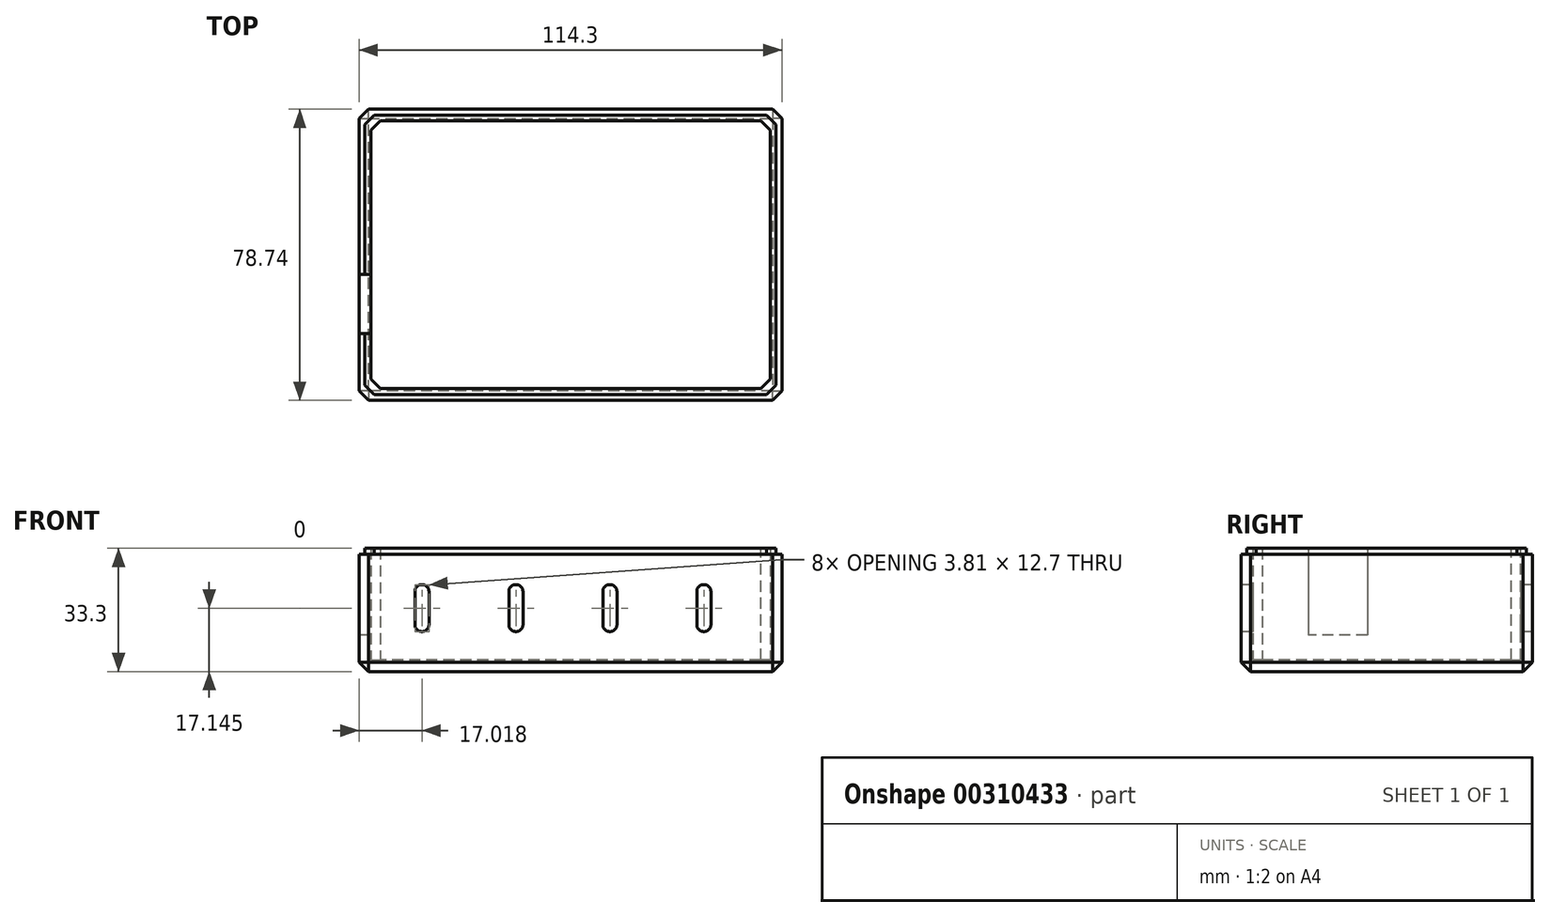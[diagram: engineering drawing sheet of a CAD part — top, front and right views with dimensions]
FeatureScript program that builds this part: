
annotation { "Feature Type Name" : "Feature", "Feature Type Description" : "" }
export const myFeature = defineFeature(function(context is Context, id is Id, definition is map)
    precondition{}
    {
        {
            var Q0;
            Q0=qCreatedBy(makeId("Top.planeOp"),FACE);
            var sketch = newSketch(context, id + "F0", { "sketchPlane" : qUnion([Q0])});
            skLineSegment(sketch, "E0.bottom", {"start": v(57.15, 39.37) * mm, "end": v(-57.15, 39.37) * mm});
            skLineSegment(sketch, "E0.top", {"start": v(57.15, -39.37) * mm, "end": v(-57.15, -39.37) * mm});
            skLineSegment(sketch, "E0.left", {"start": v(57.15, 39.37) * mm, "end": v(57.15, -39.37) * mm});
            skLineSegment(sketch, "E0.right", {"start": v(-57.15, 39.37) * mm, "end": v(-57.15, -39.37) * mm});
            skPoint(sketch, "E0.middle", {"position": v(0, 0) * mm});
            skSolve(sketch);
        }
        {
            var Q0;
            Q0 = qSketchRegion(id + "F0", true);
            extrude(context, id + "F1", {"entities" : qUnion([Q0]), "depth" : 3.17 * mm});
        }
        {
            var Q0;
            Q0=makeQuery(id+"F1.opExtrude","CAP_FACE",FACE,{"disambiguationData":[OSD([sQuery(id+"F0.wireOp",EDGE,"E0.bottom"),sQuery(id+"F0.wireOp",EDGE,"E0.top"),sQuery(id+"F0.wireOp",EDGE,"E0.left"),sQuery(id+"F0.wireOp",EDGE,"E0.right")])],"isStart":false});
            var sketch = newSketch(context, id + "F2", { "sketchPlane" : qUnion([Q0])});
            skLineSegment(sketch, "E1.0", {"start": v(53.98, 36.2) * mm, "end": v(-53.98, 36.2) * mm});
            skLineSegment(sketch, "E1.1", {"start": v(53.98, 36.2) * mm, "end": v(53.98, -36.2) * mm});
            skLineSegment(sketch, "E1.2", {"start": v(53.98, -36.2) * mm, "end": v(-53.98, -36.2) * mm});
            skLineSegment(sketch, "E1.3", {"start": v(-53.98, 36.2) * mm, "end": v(-53.98, -36.2) * mm});
            skSolve(sketch);
        }
        {
            var Q0;
            Q0=makeQuery(id+"F2.imprint","IMPRINT",FACE,{"disambiguationData":[TD([[makeQuery(id+"F2.imprint","IMPRINT",EDGE,{"derivedFrom":sQuery(id+"F2.wireOp",EDGE,"E1.0")}),-1.0]])]});
            extrude(context, id + "F3", {"entities" : qUnion([Q0]), "operationType" : NewBodyOperationType.ADD, "depth" : 28.57 * mm});
        }
        {
            var Q0;
            {var subQ0=sQuery(id+"F0.wireOp",EDGE,"E0.right");Q0=makeQuery(id+"F3.boolean.opBoolean","MERGE",FACE,{"derivedFrom":[makeQuery(id+"F1.opExtrude","SWEPT_FACE",FACE,{"disambiguationData":[OSD([subQ0])]}),makeQuery(id+"F3.opExtrude","SWEPT_FACE",FACE,{"disambiguationData":[OSD([subQ0])]})]});}
            var sketch = newSketch(context, id + "F4", { "sketchPlane" : qUnion([Q0])});
            skPoint(sketch, "E2", {"position": v(13.23, 20.83) * mm});
            skLineSegment(sketch, "E3.bottom", {"start": v(5.23, 31.75) * mm, "end": v(21.23, 31.75) * mm});
            skLineSegment(sketch, "E3.top", {"start": v(5.23, 9.9) * mm, "end": v(21.23, 9.9) * mm});
            skLineSegment(sketch, "E3.left", {"start": v(5.23, 31.75) * mm, "end": v(5.23, 9.9) * mm});
            skLineSegment(sketch, "E3.right", {"start": v(21.23, 31.75) * mm, "end": v(21.23, 9.9) * mm});
            skSolve(sketch);
        }
        {
            var Q0;
            Q0=makeQuery(id+"F4.imprint","IMPRINT",FACE,{"disambiguationData":[TD([[makeQuery(id+"F4.imprint","IMPRINT",EDGE,{"derivedFrom":sQuery(id+"F4.wireOp",EDGE,"E3.bottom")}),-1.0]])]});
            extrude(context, id + "F5", {"entities" : qUnion([Q0]), "operationType" : NewBodyOperationType.REMOVE, "endBound" : BoundingType.UP_TO_NEXT, "oppositeDirection" : true, "depth" : 25.4 * mm});
        }
        {
            var Q0;
            Q0=makeQuery(id+"F3.opExtrude","CAP_FACE",FACE,{"disambiguationData":[OSD([sQuery(id+"F0.wireOp",EDGE,"E0.bottom"),sQuery(id+"F0.wireOp",EDGE,"E0.top"),sQuery(id+"F0.wireOp",EDGE,"E0.left"),sQuery(id+"F0.wireOp",EDGE,"E0.right"),sQuery(id+"F2.wireOp",EDGE,"E1.0"),sQuery(id+"F2.wireOp",EDGE,"E1.1"),sQuery(id+"F2.wireOp",EDGE,"E1.2"),sQuery(id+"F2.wireOp",EDGE,"E1.3")])],"isStart":false});
            var sketch = newSketch(context, id + "F6", { "sketchPlane" : qUnion([Q0])});
            skLineSegment(sketch, "E4.0", {"start": v(-55.55, 37.77) * mm, "end": v(-55.55, -5.23) * mm});
            skLineSegment(sketch, "E4.1", {"start": v(-55.55, -21.23) * mm, "end": v(-55.55, -37.77) * mm});
            skLineSegment(sketch, "E4.2", {"start": v(55.55, -37.77) * mm, "end": v(-55.55, -37.77) * mm});
            skLineSegment(sketch, "E4.3", {"start": v(55.55, 37.77) * mm, "end": v(55.55, -37.77) * mm});
            skLineSegment(sketch, "E4.4", {"start": v(55.55, 37.77) * mm, "end": v(-55.55, 37.77) * mm});
            skSolve(sketch);
        }
        {
            var Q0;
            {var subQ10=sQuery(id+"F6.wireOp",EDGE,"E4.0");Q0=makeQuery(id+"F6.imprint","IMPRINT",FACE,{"disambiguationData":[TD([[makeQuery(id+"F6.imprint","IMPRINT",EDGE,{"derivedFrom":subQ10}),1.0]])]});}
            extrude(context, id + "F7", {"entities" : qUnion([Q0]), "operationType" : NewBodyOperationType.ADD, "depth" : 1.55 * mm});
        }
        {
            var Q0;
            {var subQ0=sQuery(id+"F0.wireOp",EDGE,"E0.left");var subQ1=sQuery(id+"F0.wireOp",EDGE,"E0.bottom");Q0=makeQuery(id+"F3.boolean.opBoolean","MERGE",EDGE,{"derivedFrom":[makeQuery(id+"F1.opExtrude","SWEPT_EDGE",EDGE,{"disambiguationData":[OSD([subQ1,subQ0])]}),makeQuery(id+"F3.opExtrude","SWEPT_EDGE",EDGE,{"disambiguationData":[OSD([subQ1,subQ0])]})]});}
            var Q1;
            {var subQ0=sQuery(id+"F0.wireOp",EDGE,"E0.left");var subQ1=sQuery(id+"F0.wireOp",EDGE,"E0.top");Q1=makeQuery(id+"F3.boolean.opBoolean","MERGE",EDGE,{"derivedFrom":[makeQuery(id+"F1.opExtrude","SWEPT_EDGE",EDGE,{"disambiguationData":[OSD([subQ1,subQ0])]}),makeQuery(id+"F3.opExtrude","SWEPT_EDGE",EDGE,{"disambiguationData":[OSD([subQ1,subQ0])]})]});}
            var Q2;
            {var subQ0=sQuery(id+"F0.wireOp",EDGE,"E0.right");var subQ1=sQuery(id+"F0.wireOp",EDGE,"E0.top");Q2=makeQuery(id+"F3.boolean.opBoolean","MERGE",EDGE,{"derivedFrom":[makeQuery(id+"F1.opExtrude","SWEPT_EDGE",EDGE,{"disambiguationData":[OSD([subQ1,subQ0])]}),makeQuery(id+"F3.opExtrude","SWEPT_EDGE",EDGE,{"disambiguationData":[OSD([subQ1,subQ0])]})]});}
            var Q3;
            {var subQ0=sQuery(id+"F0.wireOp",EDGE,"E0.right");var subQ1=sQuery(id+"F0.wireOp",EDGE,"E0.bottom");Q3=makeQuery(id+"F3.boolean.opBoolean","MERGE",EDGE,{"derivedFrom":[makeQuery(id+"F1.opExtrude","SWEPT_EDGE",EDGE,{"disambiguationData":[OSD([subQ1,subQ0])]}),makeQuery(id+"F3.opExtrude","SWEPT_EDGE",EDGE,{"disambiguationData":[OSD([subQ1,subQ0])]})]});}
            var Q4;
            Q4=makeQuery(id+"F1.opExtrude","CAP_EDGE",EDGE,{"disambiguationData":[OSD([sQuery(id+"F0.wireOp",EDGE,"E0.bottom")])],"isStart":true});
            var Q5;
            Q5=makeQuery(id+"F1.opExtrude","CAP_EDGE",EDGE,{"disambiguationData":[OSD([sQuery(id+"F0.wireOp",EDGE,"E0.right")])],"isStart":true});
            var Q6;
            Q6=makeQuery(id+"F1.opExtrude","CAP_EDGE",EDGE,{"disambiguationData":[OSD([sQuery(id+"F0.wireOp",EDGE,"E0.top")])],"isStart":true});
            var Q7;
            Q7=makeQuery(id+"F1.opExtrude","CAP_EDGE",EDGE,{"disambiguationData":[OSD([sQuery(id+"F0.wireOp",EDGE,"E0.left")])],"isStart":true});
            chamfer(context, id + "F8", {"entities" : qUnion([Q0, Q1, Q2, Q3, Q4, Q5, Q6, Q7]), "width" : 2.54 * mm, "tangentPropagation" : true});
        }
        {
            var Q0;
            {var subQ0=sQuery(id+"F2.wireOp",EDGE,"E1.3");var subQ1=sQuery(id+"F2.wireOp",EDGE,"E1.0");Q0=makeQuery(id+"F7.boolean.opBoolean","MERGE",EDGE,{"derivedFrom":[makeQuery(id+"F3.opExtrude","SWEPT_EDGE",EDGE,{"disambiguationData":[OSD([subQ1,subQ0])]}),makeQuery(id+"F7.opExtrude","SWEPT_EDGE",EDGE,{"disambiguationData":[OSD([subQ1,subQ0])]})]});}
            var Q1;
            {var subQ0=sQuery(id+"F2.wireOp",EDGE,"E1.1");var subQ1=sQuery(id+"F2.wireOp",EDGE,"E1.0");Q1=makeQuery(id+"F7.boolean.opBoolean","MERGE",EDGE,{"derivedFrom":[makeQuery(id+"F3.opExtrude","SWEPT_EDGE",EDGE,{"disambiguationData":[OSD([subQ1,subQ0])]}),makeQuery(id+"F7.opExtrude","SWEPT_EDGE",EDGE,{"disambiguationData":[OSD([subQ1,subQ0])]})]});}
            var Q2;
            {var subQ0=sQuery(id+"F2.wireOp",EDGE,"E1.2");var subQ1=sQuery(id+"F2.wireOp",EDGE,"E1.1");Q2=makeQuery(id+"F7.boolean.opBoolean","MERGE",EDGE,{"derivedFrom":[makeQuery(id+"F3.opExtrude","SWEPT_EDGE",EDGE,{"disambiguationData":[OSD([subQ1,subQ0])]}),makeQuery(id+"F7.opExtrude","SWEPT_EDGE",EDGE,{"disambiguationData":[OSD([subQ1,subQ0])]})]});}
            var Q3;
            {var subQ0=sQuery(id+"F2.wireOp",EDGE,"E1.3");var subQ1=sQuery(id+"F2.wireOp",EDGE,"E1.2");Q3=makeQuery(id+"F7.boolean.opBoolean","MERGE",EDGE,{"derivedFrom":[makeQuery(id+"F3.opExtrude","SWEPT_EDGE",EDGE,{"disambiguationData":[OSD([subQ1,subQ0])]}),makeQuery(id+"F7.opExtrude","SWEPT_EDGE",EDGE,{"disambiguationData":[OSD([subQ1,subQ0])]})]});}
            chamfer(context, id + "F9", {"entities" : qUnion([Q0, Q1, Q2, Q3]), "width" : 2.54 * mm, "tangentPropagation" : true});
        }
        {
            var Q0;
            Q0=makeQuery(id+"F7.opExtrude","SWEPT_EDGE",EDGE,{"disambiguationData":[OSD([sQuery(id+"F6.wireOp",EDGE,"E4.3"),sQuery(id+"F6.wireOp",EDGE,"E4.4")])]});
            var Q1;
            Q1=makeQuery(id+"F7.opExtrude","SWEPT_EDGE",EDGE,{"disambiguationData":[OSD([sQuery(id+"F6.wireOp",EDGE,"E4.0"),sQuery(id+"F6.wireOp",EDGE,"E4.4")])]});
            var Q2;
            Q2=makeQuery(id+"F7.opExtrude","SWEPT_EDGE",EDGE,{"disambiguationData":[OSD([sQuery(id+"F6.wireOp",EDGE,"E4.1"),sQuery(id+"F6.wireOp",EDGE,"E4.2")])]});
            var Q3;
            Q3=makeQuery(id+"F7.opExtrude","SWEPT_EDGE",EDGE,{"disambiguationData":[OSD([sQuery(id+"F6.wireOp",EDGE,"E4.2"),sQuery(id+"F6.wireOp",EDGE,"E4.3")])]});
            chamfer(context, id + "F10", {"entities" : qUnion([Q0, Q1, Q2, Q3]), "width" : 2.54 * mm, "tangentPropagation" : true});
        }
        {
            var Q0;
            {var subQ0=sQuery(id+"F0.wireOp",EDGE,"E0.top");Q0=makeQuery(id+"F3.boolean.opBoolean","MERGE",FACE,{"derivedFrom":[makeQuery(id+"F1.opExtrude","SWEPT_FACE",FACE,{"disambiguationData":[OSD([subQ0])]}),makeQuery(id+"F3.opExtrude","SWEPT_FACE",FACE,{"disambiguationData":[OSD([subQ0])]})]});}
            var sketch = newSketch(context, id + "F11", { "sketchPlane" : qUnion([Q0])});
            skPoint(sketch, "E5", {"position": v(-40.13, 17.14) * mm});
            skPoint(sketch, "E6", {"position": v(-14.73, 17.14) * mm});
            skPoint(sketch, "E7", {"position": v(10.67, 17.14) * mm});
            skPoint(sketch, "E8", {"position": v(36.07, 17.14) * mm});
            skLineSegment(sketch, "E9.bottom", {"start": v(-42.04, 23.5) * mm, "end": v(-38.23, 23.5) * mm});
            skLineSegment(sketch, "E9.top", {"start": v(-42.04, 10.8) * mm, "end": v(-38.23, 10.8) * mm});
            skLineSegment(sketch, "E9.left", {"start": v(-42.04, 23.5) * mm, "end": v(-42.04, 10.8) * mm});
            skLineSegment(sketch, "E9.right", {"start": v(-38.23, 23.5) * mm, "end": v(-38.23, 10.8) * mm});
            skLineSegment(sketch, "E10.bottom", {"start": v(-16.64, 23.5) * mm, "end": v(-12.83, 23.5) * mm});
            skLineSegment(sketch, "E10.top", {"start": v(-16.64, 10.8) * mm, "end": v(-12.83, 10.8) * mm});
            skLineSegment(sketch, "E10.left", {"start": v(-16.64, 23.5) * mm, "end": v(-16.64, 10.8) * mm});
            skLineSegment(sketch, "E10.right", {"start": v(-12.83, 23.5) * mm, "end": v(-12.83, 10.8) * mm});
            skLineSegment(sketch, "E11.bottom", {"start": v(8.76, 23.5) * mm, "end": v(12.57, 23.5) * mm});
            skLineSegment(sketch, "E11.top", {"start": v(8.76, 10.8) * mm, "end": v(12.57, 10.8) * mm});
            skLineSegment(sketch, "E11.left", {"start": v(8.76, 23.5) * mm, "end": v(8.76, 10.8) * mm});
            skLineSegment(sketch, "E11.right", {"start": v(12.57, 23.5) * mm, "end": v(12.57, 10.8) * mm});
            skLineSegment(sketch, "E12.bottom", {"start": v(34.16, 23.5) * mm, "end": v(37.97, 23.5) * mm});
            skLineSegment(sketch, "E12.top", {"start": v(34.16, 10.8) * mm, "end": v(37.97, 10.8) * mm});
            skLineSegment(sketch, "E12.left", {"start": v(34.16, 23.5) * mm, "end": v(34.16, 10.8) * mm});
            skLineSegment(sketch, "E12.right", {"start": v(37.97, 23.5) * mm, "end": v(37.97, 10.8) * mm});
            skSolve(sketch);
        }
        {
            var Q0;
            Q0=makeQuery(id+"F11.imprint","IMPRINT",FACE,{"disambiguationData":[TD([[makeQuery(id+"F11.imprint","IMPRINT",EDGE,{"derivedFrom":sQuery(id+"F11.wireOp",EDGE,"E9.bottom")}),-1.0]])]});
            var Q1;
            Q1=makeQuery(id+"F11.imprint","IMPRINT",FACE,{"disambiguationData":[TD([[makeQuery(id+"F11.imprint","IMPRINT",EDGE,{"derivedFrom":sQuery(id+"F11.wireOp",EDGE,"E10.bottom")}),-1.0]])]});
            var Q2;
            Q2=makeQuery(id+"F11.imprint","IMPRINT",FACE,{"disambiguationData":[TD([[makeQuery(id+"F11.imprint","IMPRINT",EDGE,{"derivedFrom":sQuery(id+"F11.wireOp",EDGE,"E11.bottom")}),-1.0]])]});
            var Q3;
            Q3=makeQuery(id+"F11.imprint","IMPRINT",FACE,{"disambiguationData":[TD([[makeQuery(id+"F11.imprint","IMPRINT",EDGE,{"derivedFrom":sQuery(id+"F11.wireOp",EDGE,"E12.bottom")}),-1.0]])]});
            extrude(context, id + "F12", {"entities" : qUnion([Q0, Q1, Q2, Q3]), "operationType" : NewBodyOperationType.REMOVE, "endBound" : BoundingType.THROUGH_ALL, "oppositeDirection" : true, "depth" : 25.4 * mm});
        }
        {
            var Q0;
            {var subQ1=sQuery(id+"F0.wireOp",EDGE,"E0.top");var subQ2=sQuery(id+"F11.wireOp",EDGE,"E9.bottom");var subQ3=sQuery(id+"F11.wireOp",EDGE,"E9.left");Q0=makeQuery(id+"F12.boolean.opBoolean","COPY",EDGE,{"disambiguationData":[TD([makeQuery(id+"F1.opExtrude","SWEPT_FACE",FACE,{"disambiguationData":[OSD([subQ1])]})])],"derivedFrom":makeQuery(id+"F12.opExtrude","SWEPT_EDGE",EDGE,{"disambiguationData":[OSD([subQ2,subQ3])]})});}
            var Q1;
            {var subQ1=sQuery(id+"F0.wireOp",EDGE,"E0.top");var subQ2=sQuery(id+"F11.wireOp",EDGE,"E10.left");var subQ3=sQuery(id+"F11.wireOp",EDGE,"E10.bottom");Q1=makeQuery(id+"F12.boolean.opBoolean","COPY",EDGE,{"disambiguationData":[TD([makeQuery(id+"F1.opExtrude","SWEPT_FACE",FACE,{"disambiguationData":[OSD([subQ1])]})])],"derivedFrom":makeQuery(id+"F12.opExtrude","SWEPT_EDGE",EDGE,{"disambiguationData":[OSD([subQ3,subQ2])]})});}
            var Q2;
            {var subQ1=sQuery(id+"F0.wireOp",EDGE,"E0.top");var subQ2=sQuery(id+"F11.wireOp",EDGE,"E11.bottom");var subQ3=sQuery(id+"F11.wireOp",EDGE,"E11.left");Q2=makeQuery(id+"F12.boolean.opBoolean","COPY",EDGE,{"disambiguationData":[TD([makeQuery(id+"F1.opExtrude","SWEPT_FACE",FACE,{"disambiguationData":[OSD([subQ1])]})])],"derivedFrom":makeQuery(id+"F12.opExtrude","SWEPT_EDGE",EDGE,{"disambiguationData":[OSD([subQ2,subQ3])]})});}
            var Q3;
            {var subQ1=sQuery(id+"F0.wireOp",EDGE,"E0.top");var subQ2=sQuery(id+"F11.wireOp",EDGE,"E12.bottom");var subQ3=sQuery(id+"F11.wireOp",EDGE,"E12.left");Q3=makeQuery(id+"F12.boolean.opBoolean","COPY",EDGE,{"disambiguationData":[TD([makeQuery(id+"F1.opExtrude","SWEPT_FACE",FACE,{"disambiguationData":[OSD([subQ1])]})])],"derivedFrom":makeQuery(id+"F12.opExtrude","SWEPT_EDGE",EDGE,{"disambiguationData":[OSD([subQ2,subQ3])]})});}
            var Q4;
            {var subQ1=sQuery(id+"F0.wireOp",EDGE,"E0.top");var subQ2=sQuery(id+"F11.wireOp",EDGE,"E9.bottom");var subQ3=sQuery(id+"F11.wireOp",EDGE,"E9.right");Q4=makeQuery(id+"F12.boolean.opBoolean","COPY",EDGE,{"disambiguationData":[TD([makeQuery(id+"F1.opExtrude","SWEPT_FACE",FACE,{"disambiguationData":[OSD([subQ1])]})])],"derivedFrom":makeQuery(id+"F12.opExtrude","SWEPT_EDGE",EDGE,{"disambiguationData":[OSD([subQ2,subQ3])]})});}
            var Q5;
            {var subQ1=sQuery(id+"F0.wireOp",EDGE,"E0.top");var subQ2=sQuery(id+"F11.wireOp",EDGE,"E10.bottom");var subQ3=sQuery(id+"F11.wireOp",EDGE,"E10.right");Q5=makeQuery(id+"F12.boolean.opBoolean","COPY",EDGE,{"disambiguationData":[TD([makeQuery(id+"F1.opExtrude","SWEPT_FACE",FACE,{"disambiguationData":[OSD([subQ1])]})])],"derivedFrom":makeQuery(id+"F12.opExtrude","SWEPT_EDGE",EDGE,{"disambiguationData":[OSD([subQ2,subQ3])]})});}
            var Q6;
            {var subQ1=sQuery(id+"F0.wireOp",EDGE,"E0.top");var subQ2=sQuery(id+"F11.wireOp",EDGE,"E11.bottom");var subQ3=sQuery(id+"F11.wireOp",EDGE,"E11.right");Q6=makeQuery(id+"F12.boolean.opBoolean","COPY",EDGE,{"disambiguationData":[TD([makeQuery(id+"F1.opExtrude","SWEPT_FACE",FACE,{"disambiguationData":[OSD([subQ1])]})])],"derivedFrom":makeQuery(id+"F12.opExtrude","SWEPT_EDGE",EDGE,{"disambiguationData":[OSD([subQ2,subQ3])]})});}
            var Q7;
            {var subQ1=sQuery(id+"F0.wireOp",EDGE,"E0.top");var subQ2=sQuery(id+"F11.wireOp",EDGE,"E12.bottom");var subQ3=sQuery(id+"F11.wireOp",EDGE,"E12.right");Q7=makeQuery(id+"F12.boolean.opBoolean","COPY",EDGE,{"disambiguationData":[TD([makeQuery(id+"F1.opExtrude","SWEPT_FACE",FACE,{"disambiguationData":[OSD([subQ1])]})])],"derivedFrom":makeQuery(id+"F12.opExtrude","SWEPT_EDGE",EDGE,{"disambiguationData":[OSD([subQ2,subQ3])]})});}
            var Q8;
            {var subQ1=sQuery(id+"F11.wireOp",EDGE,"E9.top");var subQ2=sQuery(id+"F0.wireOp",EDGE,"E0.top");var subQ3=sQuery(id+"F11.wireOp",EDGE,"E9.left");Q8=makeQuery(id+"F12.boolean.opBoolean","COPY",EDGE,{"disambiguationData":[TD([makeQuery(id+"F1.opExtrude","SWEPT_FACE",FACE,{"disambiguationData":[OSD([subQ2])]})])],"derivedFrom":makeQuery(id+"F12.opExtrude","SWEPT_EDGE",EDGE,{"disambiguationData":[OSD([subQ1,subQ3])]})});}
            var Q9;
            {var subQ1=sQuery(id+"F0.wireOp",EDGE,"E0.top");var subQ2=sQuery(id+"F11.wireOp",EDGE,"E10.left");var subQ3=sQuery(id+"F11.wireOp",EDGE,"E10.top");Q9=makeQuery(id+"F12.boolean.opBoolean","COPY",EDGE,{"disambiguationData":[TD([makeQuery(id+"F1.opExtrude","SWEPT_FACE",FACE,{"disambiguationData":[OSD([subQ1])]})])],"derivedFrom":makeQuery(id+"F12.opExtrude","SWEPT_EDGE",EDGE,{"disambiguationData":[OSD([subQ3,subQ2])]})});}
            var Q10;
            {var subQ1=sQuery(id+"F0.wireOp",EDGE,"E0.top");var subQ2=sQuery(id+"F11.wireOp",EDGE,"E11.top");var subQ3=sQuery(id+"F11.wireOp",EDGE,"E11.left");Q10=makeQuery(id+"F12.boolean.opBoolean","COPY",EDGE,{"disambiguationData":[TD([makeQuery(id+"F1.opExtrude","SWEPT_FACE",FACE,{"disambiguationData":[OSD([subQ1])]})])],"derivedFrom":makeQuery(id+"F12.opExtrude","SWEPT_EDGE",EDGE,{"disambiguationData":[OSD([subQ2,subQ3])]})});}
            var Q11;
            {var subQ1=sQuery(id+"F0.wireOp",EDGE,"E0.top");var subQ2=sQuery(id+"F11.wireOp",EDGE,"E12.top");var subQ3=sQuery(id+"F11.wireOp",EDGE,"E12.left");Q11=makeQuery(id+"F12.boolean.opBoolean","COPY",EDGE,{"disambiguationData":[TD([makeQuery(id+"F1.opExtrude","SWEPT_FACE",FACE,{"disambiguationData":[OSD([subQ1])]})])],"derivedFrom":makeQuery(id+"F12.opExtrude","SWEPT_EDGE",EDGE,{"disambiguationData":[OSD([subQ2,subQ3])]})});}
            var Q12;
            {var subQ1=sQuery(id+"F11.wireOp",EDGE,"E9.top");var subQ2=sQuery(id+"F0.wireOp",EDGE,"E0.top");var subQ3=sQuery(id+"F11.wireOp",EDGE,"E9.right");Q12=makeQuery(id+"F12.boolean.opBoolean","COPY",EDGE,{"disambiguationData":[TD([makeQuery(id+"F1.opExtrude","SWEPT_FACE",FACE,{"disambiguationData":[OSD([subQ2])]})])],"derivedFrom":makeQuery(id+"F12.opExtrude","SWEPT_EDGE",EDGE,{"disambiguationData":[OSD([subQ1,subQ3])]})});}
            var Q13;
            {var subQ1=sQuery(id+"F0.wireOp",EDGE,"E0.top");var subQ2=sQuery(id+"F11.wireOp",EDGE,"E10.top");var subQ3=sQuery(id+"F11.wireOp",EDGE,"E10.right");Q13=makeQuery(id+"F12.boolean.opBoolean","COPY",EDGE,{"disambiguationData":[TD([makeQuery(id+"F1.opExtrude","SWEPT_FACE",FACE,{"disambiguationData":[OSD([subQ1])]})])],"derivedFrom":makeQuery(id+"F12.opExtrude","SWEPT_EDGE",EDGE,{"disambiguationData":[OSD([subQ2,subQ3])]})});}
            var Q14;
            {var subQ1=sQuery(id+"F0.wireOp",EDGE,"E0.top");var subQ2=sQuery(id+"F11.wireOp",EDGE,"E11.top");var subQ3=sQuery(id+"F11.wireOp",EDGE,"E11.right");Q14=makeQuery(id+"F12.boolean.opBoolean","COPY",EDGE,{"disambiguationData":[TD([makeQuery(id+"F1.opExtrude","SWEPT_FACE",FACE,{"disambiguationData":[OSD([subQ1])]})])],"derivedFrom":makeQuery(id+"F12.opExtrude","SWEPT_EDGE",EDGE,{"disambiguationData":[OSD([subQ2,subQ3])]})});}
            var Q15;
            {var subQ1=sQuery(id+"F0.wireOp",EDGE,"E0.top");var subQ2=sQuery(id+"F11.wireOp",EDGE,"E12.top");var subQ3=sQuery(id+"F11.wireOp",EDGE,"E12.right");Q15=makeQuery(id+"F12.boolean.opBoolean","COPY",EDGE,{"disambiguationData":[TD([makeQuery(id+"F1.opExtrude","SWEPT_FACE",FACE,{"disambiguationData":[OSD([subQ1])]})])],"derivedFrom":makeQuery(id+"F12.opExtrude","SWEPT_EDGE",EDGE,{"disambiguationData":[OSD([subQ2,subQ3])]})});}
            var Q16;
            {var subQ0=sQuery(id+"F0.wireOp",EDGE,"E0.bottom");var subQ2=sQuery(id+"F11.wireOp",EDGE,"E12.right");var subQ3=sQuery(id+"F11.wireOp",EDGE,"E12.bottom");Q16=makeQuery(id+"F12.boolean.opBoolean","COPY",EDGE,{"disambiguationData":[TD([makeQuery(id+"F1.opExtrude","SWEPT_FACE",FACE,{"disambiguationData":[OSD([subQ0])]})])],"derivedFrom":makeQuery(id+"F12.opExtrude","SWEPT_EDGE",EDGE,{"disambiguationData":[OSD([subQ3,subQ2])]})});}
            var Q17;
            {var subQ0=sQuery(id+"F0.wireOp",EDGE,"E0.bottom");var subQ2=sQuery(id+"F11.wireOp",EDGE,"E11.bottom");var subQ3=sQuery(id+"F11.wireOp",EDGE,"E11.right");Q17=makeQuery(id+"F12.boolean.opBoolean","COPY",EDGE,{"disambiguationData":[TD([makeQuery(id+"F1.opExtrude","SWEPT_FACE",FACE,{"disambiguationData":[OSD([subQ0])]})])],"derivedFrom":makeQuery(id+"F12.opExtrude","SWEPT_EDGE",EDGE,{"disambiguationData":[OSD([subQ2,subQ3])]})});}
            var Q18;
            {var subQ0=sQuery(id+"F0.wireOp",EDGE,"E0.bottom");var subQ2=sQuery(id+"F11.wireOp",EDGE,"E10.bottom");var subQ3=sQuery(id+"F11.wireOp",EDGE,"E10.right");Q18=makeQuery(id+"F12.boolean.opBoolean","COPY",EDGE,{"disambiguationData":[TD([makeQuery(id+"F1.opExtrude","SWEPT_FACE",FACE,{"disambiguationData":[OSD([subQ0])]})])],"derivedFrom":makeQuery(id+"F12.opExtrude","SWEPT_EDGE",EDGE,{"disambiguationData":[OSD([subQ2,subQ3])]})});}
            var Q19;
            {var subQ0=sQuery(id+"F0.wireOp",EDGE,"E0.bottom");var subQ2=sQuery(id+"F11.wireOp",EDGE,"E9.right");var subQ3=sQuery(id+"F11.wireOp",EDGE,"E9.bottom");Q19=makeQuery(id+"F12.boolean.opBoolean","COPY",EDGE,{"disambiguationData":[TD([makeQuery(id+"F1.opExtrude","SWEPT_FACE",FACE,{"disambiguationData":[OSD([subQ0])]})])],"derivedFrom":makeQuery(id+"F12.opExtrude","SWEPT_EDGE",EDGE,{"disambiguationData":[OSD([subQ3,subQ2])]})});}
            var Q20;
            {var subQ0=sQuery(id+"F0.wireOp",EDGE,"E0.bottom");var subQ2=sQuery(id+"F11.wireOp",EDGE,"E12.bottom");var subQ3=sQuery(id+"F11.wireOp",EDGE,"E12.left");Q20=makeQuery(id+"F12.boolean.opBoolean","COPY",EDGE,{"disambiguationData":[TD([makeQuery(id+"F1.opExtrude","SWEPT_FACE",FACE,{"disambiguationData":[OSD([subQ0])]})])],"derivedFrom":makeQuery(id+"F12.opExtrude","SWEPT_EDGE",EDGE,{"disambiguationData":[OSD([subQ2,subQ3])]})});}
            var Q21;
            {var subQ0=sQuery(id+"F0.wireOp",EDGE,"E0.bottom");var subQ2=sQuery(id+"F11.wireOp",EDGE,"E11.bottom");var subQ3=sQuery(id+"F11.wireOp",EDGE,"E11.left");Q21=makeQuery(id+"F12.boolean.opBoolean","COPY",EDGE,{"disambiguationData":[TD([makeQuery(id+"F1.opExtrude","SWEPT_FACE",FACE,{"disambiguationData":[OSD([subQ0])]})])],"derivedFrom":makeQuery(id+"F12.opExtrude","SWEPT_EDGE",EDGE,{"disambiguationData":[OSD([subQ2,subQ3])]})});}
            var Q22;
            {var subQ0=sQuery(id+"F0.wireOp",EDGE,"E0.bottom");var subQ2=sQuery(id+"F11.wireOp",EDGE,"E10.bottom");var subQ3=sQuery(id+"F11.wireOp",EDGE,"E10.left");Q22=makeQuery(id+"F12.boolean.opBoolean","COPY",EDGE,{"disambiguationData":[TD([makeQuery(id+"F1.opExtrude","SWEPT_FACE",FACE,{"disambiguationData":[OSD([subQ0])]})])],"derivedFrom":makeQuery(id+"F12.opExtrude","SWEPT_EDGE",EDGE,{"disambiguationData":[OSD([subQ2,subQ3])]})});}
            var Q23;
            {var subQ0=sQuery(id+"F0.wireOp",EDGE,"E0.bottom");var subQ2=sQuery(id+"F11.wireOp",EDGE,"E9.bottom");var subQ3=sQuery(id+"F11.wireOp",EDGE,"E9.left");Q23=makeQuery(id+"F12.boolean.opBoolean","COPY",EDGE,{"disambiguationData":[TD([makeQuery(id+"F1.opExtrude","SWEPT_FACE",FACE,{"disambiguationData":[OSD([subQ0])]})])],"derivedFrom":makeQuery(id+"F12.opExtrude","SWEPT_EDGE",EDGE,{"disambiguationData":[OSD([subQ2,subQ3])]})});}
            var Q24;
            {var subQ0=sQuery(id+"F0.wireOp",EDGE,"E0.bottom");var subQ2=sQuery(id+"F11.wireOp",EDGE,"E12.top");var subQ3=sQuery(id+"F11.wireOp",EDGE,"E12.left");Q24=makeQuery(id+"F12.boolean.opBoolean","COPY",EDGE,{"disambiguationData":[TD([makeQuery(id+"F1.opExtrude","SWEPT_FACE",FACE,{"disambiguationData":[OSD([subQ0])]})])],"derivedFrom":makeQuery(id+"F12.opExtrude","SWEPT_EDGE",EDGE,{"disambiguationData":[OSD([subQ2,subQ3])]})});}
            var Q25;
            {var subQ0=sQuery(id+"F0.wireOp",EDGE,"E0.bottom");var subQ2=sQuery(id+"F11.wireOp",EDGE,"E11.left");var subQ3=sQuery(id+"F11.wireOp",EDGE,"E11.top");Q25=makeQuery(id+"F12.boolean.opBoolean","COPY",EDGE,{"disambiguationData":[TD([makeQuery(id+"F1.opExtrude","SWEPT_FACE",FACE,{"disambiguationData":[OSD([subQ0])]})])],"derivedFrom":makeQuery(id+"F12.opExtrude","SWEPT_EDGE",EDGE,{"disambiguationData":[OSD([subQ3,subQ2])]})});}
            var Q26;
            {var subQ0=sQuery(id+"F0.wireOp",EDGE,"E0.bottom");var subQ2=sQuery(id+"F11.wireOp",EDGE,"E10.top");var subQ3=sQuery(id+"F11.wireOp",EDGE,"E10.left");Q26=makeQuery(id+"F12.boolean.opBoolean","COPY",EDGE,{"disambiguationData":[TD([makeQuery(id+"F1.opExtrude","SWEPT_FACE",FACE,{"disambiguationData":[OSD([subQ0])]})])],"derivedFrom":makeQuery(id+"F12.opExtrude","SWEPT_EDGE",EDGE,{"disambiguationData":[OSD([subQ2,subQ3])]})});}
            var Q27;
            {var subQ0=sQuery(id+"F0.wireOp",EDGE,"E0.bottom");var subQ2=sQuery(id+"F11.wireOp",EDGE,"E9.top");var subQ3=sQuery(id+"F11.wireOp",EDGE,"E9.left");Q27=makeQuery(id+"F12.boolean.opBoolean","COPY",EDGE,{"disambiguationData":[TD([makeQuery(id+"F1.opExtrude","SWEPT_FACE",FACE,{"disambiguationData":[OSD([subQ0])]})])],"derivedFrom":makeQuery(id+"F12.opExtrude","SWEPT_EDGE",EDGE,{"disambiguationData":[OSD([subQ2,subQ3])]})});}
            var Q28;
            {var subQ0=sQuery(id+"F0.wireOp",EDGE,"E0.bottom");var subQ2=sQuery(id+"F11.wireOp",EDGE,"E9.right");var subQ3=sQuery(id+"F11.wireOp",EDGE,"E9.top");Q28=makeQuery(id+"F12.boolean.opBoolean","COPY",EDGE,{"disambiguationData":[TD([makeQuery(id+"F1.opExtrude","SWEPT_FACE",FACE,{"disambiguationData":[OSD([subQ0])]})])],"derivedFrom":makeQuery(id+"F12.opExtrude","SWEPT_EDGE",EDGE,{"disambiguationData":[OSD([subQ3,subQ2])]})});}
            var Q29;
            {var subQ0=sQuery(id+"F0.wireOp",EDGE,"E0.bottom");var subQ2=sQuery(id+"F11.wireOp",EDGE,"E10.top");var subQ3=sQuery(id+"F11.wireOp",EDGE,"E10.right");Q29=makeQuery(id+"F12.boolean.opBoolean","COPY",EDGE,{"disambiguationData":[TD([makeQuery(id+"F1.opExtrude","SWEPT_FACE",FACE,{"disambiguationData":[OSD([subQ0])]})])],"derivedFrom":makeQuery(id+"F12.opExtrude","SWEPT_EDGE",EDGE,{"disambiguationData":[OSD([subQ2,subQ3])]})});}
            var Q30;
            {var subQ0=sQuery(id+"F0.wireOp",EDGE,"E0.bottom");var subQ2=sQuery(id+"F11.wireOp",EDGE,"E11.right");var subQ3=sQuery(id+"F11.wireOp",EDGE,"E11.top");Q30=makeQuery(id+"F12.boolean.opBoolean","COPY",EDGE,{"disambiguationData":[TD([makeQuery(id+"F1.opExtrude","SWEPT_FACE",FACE,{"disambiguationData":[OSD([subQ0])]})])],"derivedFrom":makeQuery(id+"F12.opExtrude","SWEPT_EDGE",EDGE,{"disambiguationData":[OSD([subQ3,subQ2])]})});}
            var Q31;
            {var subQ0=sQuery(id+"F0.wireOp",EDGE,"E0.bottom");var subQ2=sQuery(id+"F11.wireOp",EDGE,"E12.right");var subQ3=sQuery(id+"F11.wireOp",EDGE,"E12.top");Q31=makeQuery(id+"F12.boolean.opBoolean","COPY",EDGE,{"disambiguationData":[TD([makeQuery(id+"F1.opExtrude","SWEPT_FACE",FACE,{"disambiguationData":[OSD([subQ0])]})])],"derivedFrom":makeQuery(id+"F12.opExtrude","SWEPT_EDGE",EDGE,{"disambiguationData":[OSD([subQ3,subQ2])]})});}
            fillet(context, id + "F13", {"entities" : qUnion([Q0, Q1, Q2, Q3, Q4, Q5, Q6, Q7, Q8, Q9, Q10, Q11, Q12, Q13, Q14, Q15, Q16, Q17, Q18, Q19, Q20, Q21, Q22, Q23, Q24, Q25, Q26, Q27, Q28, Q29, Q30, Q31]), "radius" : 1.78 * mm, "tangentPropagation" : true, "allowEdgeOverflow" : false});
        }
    });
